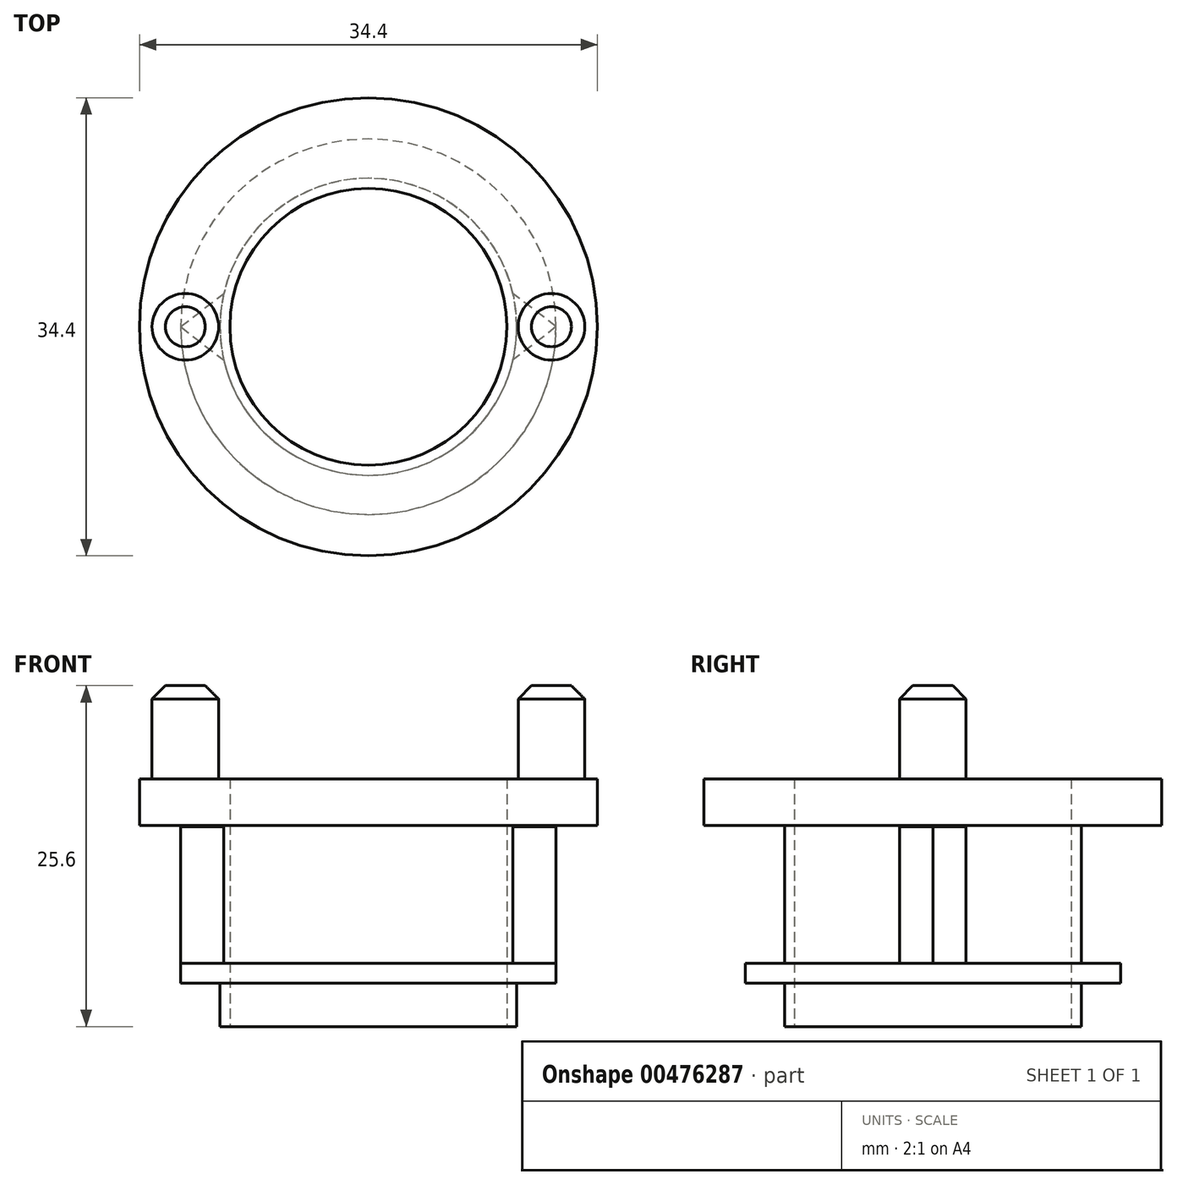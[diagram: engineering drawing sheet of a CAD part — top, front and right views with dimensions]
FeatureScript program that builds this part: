
annotation { "Feature Type Name" : "Feature", "Feature Type Description" : "" }
export const myFeature = defineFeature(function(context is Context, id is Id, definition is map)
    precondition{}
    {
        {
            var Q0;
            Q0=qCreatedBy(makeId("Top.planeOp"),FACE);
            var sketch = newSketch(context, id + "F0", { "sketchPlane" : qUnion([Q0])});
            skCircle(sketch, "E0", {"center": v(0, 0) * mm, "radius": 10.4 * mm});
            skCircle(sketch, "E1", {"center": v(0, 0) * mm, "radius": 11.15 * mm});
            skCircle(sketch, "E2", {"center": v(0, 0) * mm, "radius": 14.1 * mm});
            skSolve(sketch);
        }
        {
            var Q0;
            Q0=makeQuery(id+"F0.imprint","IMPRINT",FACE,{"disambiguationData":[TD([[makeQuery(id+"F0.imprint","IMPRINT",EDGE,{"derivedFrom":sQuery(id+"F0.wireOp",EDGE,"E0")}),-1.0]])]});
            extrude(context, id + "F1", {"entities" : qUnion([Q0]), "depth" : 18.6 * mm});
        }
        {
            var Q0;
            Q0=makeQuery(id+"F0.imprint","IMPRINT",FACE,{"disambiguationData":[TD([[makeQuery(id+"F0.imprint","IMPRINT",EDGE,{"derivedFrom":sQuery(id+"F0.wireOp",EDGE,"E1")}),-1.0]])]});
            extrude(context, id + "F2", {"entities" : qUnion([Q0]), "operationType" : NewBodyOperationType.ADD, "depth" : 4.75 * mm, "hasSecondDirection" : true, "secondDirectionOppositeDirection" : false, "secondDirectionDepth" : 3.25 * mm});
        }
        {
            var Q0;
            Q0=makeQuery(id+"F1.opExtrude","CAP_FACE",FACE,{"disambiguationData":[OSD([sQuery(id+"F0.wireOp",EDGE,"E0"),sQuery(id+"F0.wireOp",EDGE,"E1")])],"isStart":false});
            var sketch = newSketch(context, id + "F3", { "sketchPlane" : qUnion([Q0])});
            skCircle(sketch, "E3", {"center": v(0, 0) * mm, "radius": 17.2 * mm});
            skSolve(sketch);
        }
        {
            var Q0;
            Q0=makeQuery(id+"F3.imprint","IMPRINT",FACE,{"disambiguationData":[TD([[makeQuery(id+"F3.imprint","IMPRINT",EDGE,{"derivedFrom":sQuery(id+"F3.wireOp",EDGE,"E3")}),1.0]])]});
            var Q1;
            Q1=makeQuery(id+"F3.imprint","IMPRINT",FACE,{"disambiguationData":[TD([[makeQuery(id+"F3.imprint","IMPRINT",EDGE,{"derivedFrom":makeQuery(id+"F1.opExtrude","CAP_EDGE",EDGE,{"disambiguationData":[OSD([sQuery(id+"F0.wireOp",EDGE,"E0")])],"isStart":false})}),-1.0]])]});
            extrude(context, id + "F4", {"entities" : qUnion([Q0, Q1]), "operationType" : NewBodyOperationType.ADD, "oppositeDirection" : true, "depth" : 3.5 * mm});
        }
        {
            var Q0;
            {var subQ0=sQuery(id+"F0.wireOp",EDGE,"E0");Q0=makeQuery(id+"F4.boolean.opBoolean","MERGE",FACE,{"derivedFrom":[makeQuery(id+"F1.opExtrude","CAP_FACE",FACE,{"disambiguationData":[OSD([subQ0,sQuery(id+"F0.wireOp",EDGE,"E1")])],"isStart":false}),makeQuery(id+"F4.opExtrude","CAP_FACE",FACE,{"disambiguationData":[OSD([subQ0,sQuery(id+"F3.wireOp",EDGE,"E3")])],"isStart":true})]});}
            var sketch = newSketch(context, id + "F5", { "sketchPlane" : qUnion([Q0])});
            skPoint(sketch, "E4", {"position": v(0, 0) * mm});
            skCircle(sketch, "E5", {"center": v(13.75, 0) * mm, "radius": 2.5 * mm});
            skCircle(sketch, "E6.MirrorC", {"center": v(-13.75, 0) * mm, "radius": 2.5 * mm});
            skSolve(sketch);
        }
        {
            var Q0;
            Q0 = qSketchRegion(id + "F5", true);
            extrude(context, id + "F6", {"entities" : qUnion([Q0]), "operationType" : NewBodyOperationType.ADD, "depth" : 7 * mm});
        }
        {
            var Q0;
            Q0=makeQuery(id+"F6.opExtrude","CAP_EDGE",EDGE,{"disambiguationData":[OSD([sQuery(id+"F5.wireOp",EDGE,"E6.MirrorC")])],"isStart":false});
            var Q1;
            Q1=makeQuery(id+"F6.opExtrude","CAP_EDGE",EDGE,{"disambiguationData":[OSD([sQuery(id+"F5.wireOp",EDGE,"E5")])],"isStart":false});
            chamfer(context, id + "F7", {"entities" : qUnion([Q0, Q1]), "width" : 1 * mm, "tangentPropagation" : true});
        }
        {
            var Q0;
            Q0=makeQuery(id+"F2.opExtrude","CAP_FACE",FACE,{"disambiguationData":[OSD([sQuery(id+"F0.wireOp",EDGE,"E1"),sQuery(id+"F0.wireOp",EDGE,"E2")])],"isStart":false});
            var sketch = newSketch(context, id + "F8", { "sketchPlane" : qUnion([Q0])});
            skLineSegment(sketch, "E7", {"start": v(14.1, 0) * mm, "end": v(10.87, 2.5) * mm});
            skLineSegment(sketch, "E8.MirrorCS", {"start": v(14.1, 0) * mm, "end": v(10.87, -2.5) * mm});
            skCircle(sketch, "E9", {"center": v(0, 0) * mm, "radius": 11.15 * mm});
            skPoint(sketch, "E10.orphan", {"position": v(9.58, 3.5) * mm});
            skPoint(sketch, "E11.orphan", {"position": v(9.58, -3.5) * mm});
            skLineSegment(sketch, "E12.MirrorCS", {"start": v(-14.1, 0) * mm, "end": v(-10.87, -2.5) * mm});
            skLineSegment(sketch, "E13.MirrorCS", {"start": v(-14.1, 0) * mm, "end": v(-10.87, 2.5) * mm});
            skSolve(sketch);
        }
        {
            var Q0;
            {var subQ0=sQuery(id+"F8.wireOp",EDGE,"E7");Q0=makeQuery(id+"F8.imprint","IMPRINT",FACE,{"disambiguationData":[TD([[makeQuery(id+"F8.imprint","IMPRINT",EDGE,{"derivedFrom":subQ0}),1.0]])]});}
            var Q1;
            {var subQ0=sQuery(id+"F8.wireOp",EDGE,"E12.MirrorCS");Q1=makeQuery(id+"F8.imprint","IMPRINT",FACE,{"disambiguationData":[TD([[makeQuery(id+"F8.imprint","IMPRINT",EDGE,{"derivedFrom":subQ0}),1.0]])]});}
            extrude(context, id + "F9", {"entities" : qUnion([Q0, Q1]), "operationType" : NewBodyOperationType.ADD, "depth" : 10.25 * mm});
        }
    });
